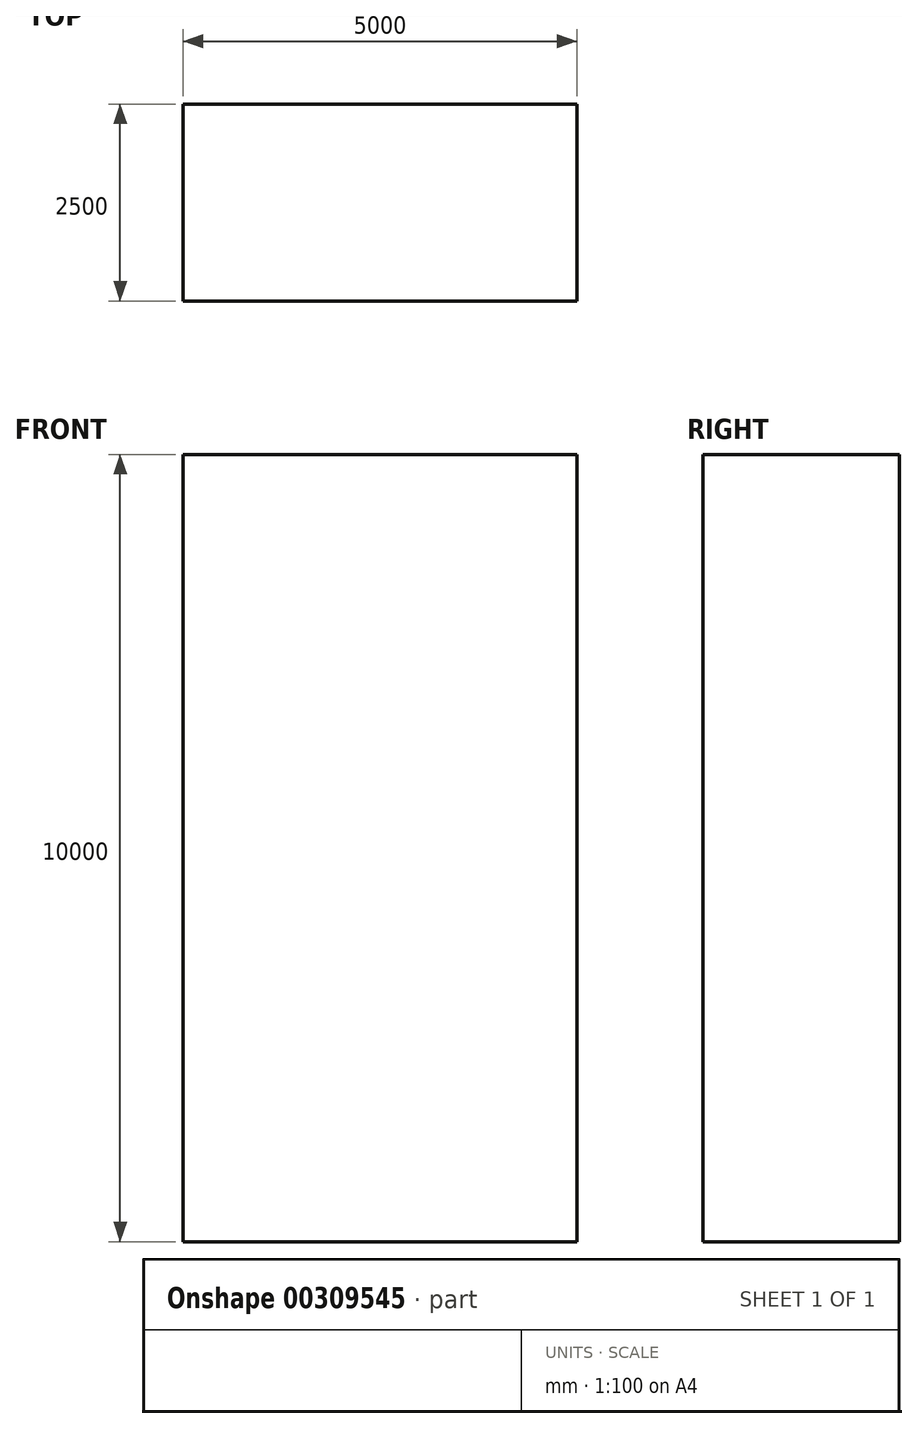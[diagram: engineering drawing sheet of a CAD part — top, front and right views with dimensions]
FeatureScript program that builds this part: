
annotation { "Feature Type Name" : "Feature", "Feature Type Description" : "" }
export const myFeature = defineFeature(function(context is Context, id is Id, definition is map)
    precondition{}
    {
        {
            var Q0;
            Q0=qCreatedBy(makeId("Front.planeOp"),FACE);
            var sketch = newSketch(context, id + "F0", { "sketchPlane" : qUnion([Q0])});
            skLineSegment(sketch, "E0.bottom", {"start": v(0, 0) * mm, "end": v(5000, 0) * mm});
            skLineSegment(sketch, "E0.top", {"start": v(0, 10000) * mm, "end": v(5000, 10000) * mm});
            skLineSegment(sketch, "E0.left", {"start": v(0, 0) * mm, "end": v(0, 10000) * mm});
            skLineSegment(sketch, "E0.right", {"start": v(5000, 0) * mm, "end": v(5000, 10000) * mm});
            skSolve(sketch);
        }
        {
            var Q0;
            Q0 = qSketchRegion(id + "F0", true);
            extrude(context, id + "F1", {"entities" : qUnion([Q0]), "depth" : 2500 * mm});
        }
    });
